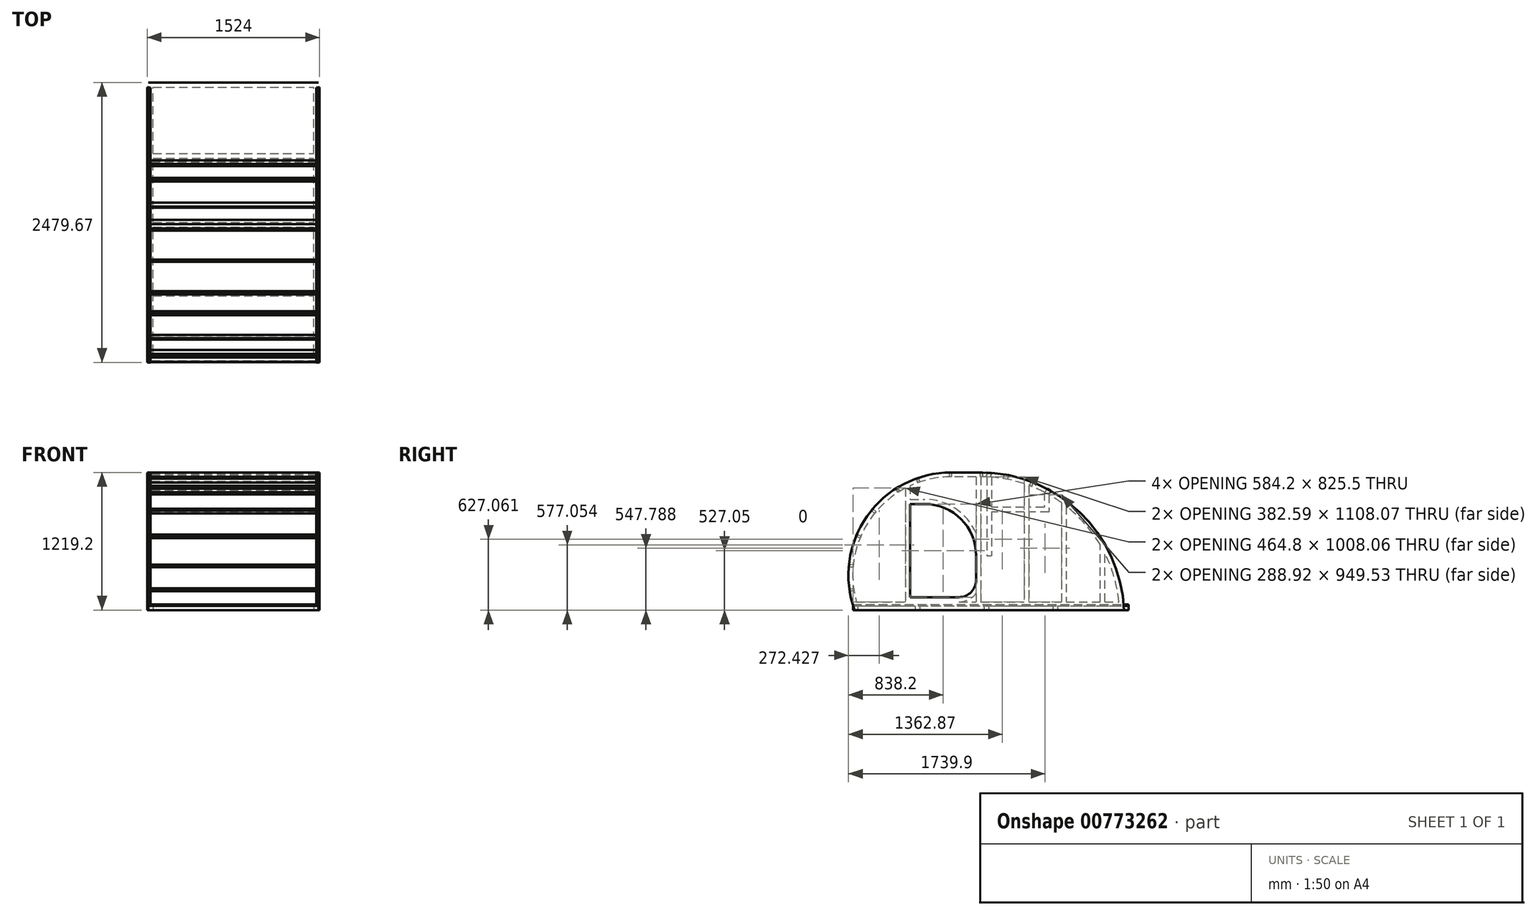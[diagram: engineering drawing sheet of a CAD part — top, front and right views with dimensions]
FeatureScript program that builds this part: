
annotation { "Feature Type Name" : "Feature", "Feature Type Description" : "" }
export const myFeature = defineFeature(function(context is Context, id is Id, definition is map)
    precondition{}
    {
        {
            var Q0;
            Q0=qCreatedBy(makeId("Right.planeOp"),FACE);
            cPlane(context, id + "F0", {"entities" : qUnion([Q0]), "cplaneType" : CPlaneType.OFFSET, "offset" : 762 * mm, "width" : 152.4 * mm, "height" : 152.4 * mm});
        }
        {
            var Q0;
            Q0=qCreatedBy(id+"F0.planeOp",FACE);
            var sketch = newSketch(context, id + "F1", { "sketchPlane" : qUnion([Q0])});
            skLineSegment(sketch, "E0", {"start": v(53.97, 0) * mm, "end": v(2438.4, 0) * mm});
            skLineSegment(sketch, "E1", {"start": v(1168.4, 1219.2) * mm, "end": v(910.4, 1219.2) * mm});
            skArc(sketch, "E2", {"start": v(910.4, 1219.2) * mm, "mid": v(165.42, 832.1) * mm, "end": v(53.97, 0) * mm});
            skLineSegment(sketch, "E3", {"start": v(0, 0) * mm, "end": v(0, 308.8) * mm, "construction": true});
            skArc(sketch, "E4", {"start": v(2438.4, 0) * mm, "mid": v(2048.65, 865.07) * mm, "end": v(1168.4, 1219.2) * mm});
            skLineSegment(sketch, "E5", {"start": v(546.1, 939.8) * mm, "end": v(546.1, 114.3) * mm});
            skLineSegment(sketch, "E6", {"start": v(546.1, 114.3) * mm, "end": v(977.9, 114.3) * mm});
            skLineSegment(sketch, "E7", {"start": v(546.1, 939.8) * mm, "end": v(673.1, 939.8) * mm});
            skLineSegment(sketch, "E8", {"start": v(1130.3, 482.6) * mm, "end": v(1130.3, 266.7) * mm});
            skArc(sketch, "E9", {"start": v(977.9, 114.3) * mm, "mid": v(1085.66, 158.94) * mm, "end": v(1130.3, 266.7) * mm});
            skArc(sketch, "E10", {"start": v(1130.3, 482.6) * mm, "mid": v(996.39, 805.89) * mm, "end": v(673.1, 939.8) * mm});
            skSolve(sketch);
        }
        {
            var Q0;
            Q0=makeQuery(id+"F1.imprint","IMPRINT",FACE,{"disambiguationData":[TD([[makeQuery(id+"F1.imprint","IMPRINT",EDGE,{"derivedFrom":sQuery(id+"F1.wireOp",EDGE,"E0")}),1.0]])]});
            extrude(context, id + "F2", {"entities" : qUnion([Q0]), "oppositeDirection" : true, "depth" : 9.52 * mm, "offsetDistance" : 25.4 * mm});
        }
        {
            var Q0;
            Q0=makeQuery(id+"F2.opExtrude","SWEPT_BODY",BODY,{"disambiguationData":[OSD([sQuery(id+"F1.wireOp",EDGE,"E0"),sQuery(id+"F1.wireOp",EDGE,"E1"),sQuery(id+"F1.wireOp",EDGE,"E2"),sQuery(id+"F1.wireOp",EDGE,"E4"),sQuery(id+"F1.wireOp",EDGE,"E5"),sQuery(id+"F1.wireOp",EDGE,"E6"),sQuery(id+"F1.wireOp",EDGE,"E7"),sQuery(id+"F1.wireOp",EDGE,"E8"),sQuery(id+"F1.wireOp",EDGE,"E9"),sQuery(id+"F1.wireOp",EDGE,"E10")])]});
            var Q1;
            Q1=qCreatedBy(makeId("Right.planeOp"),FACE);
            mirror(context, id + "F3", {"entities" : qUnion([Q0]), "mirrorPlane" : qUnion([Q1])});
        }
        {
            var Q0;
            Q0=qCreatedBy(makeId("Top.planeOp"),FACE);
            var sketch = newSketch(context, id + "F4", { "sketchPlane" : qUnion([Q0])});
            skLineSegment(sketch, "E11.bottom", {"start": v(-752.47, 41.27) * mm, "end": v(752.47, 41.27) * mm});
            skLineSegment(sketch, "E11.top", {"start": v(-752.48, 2479.68) * mm, "end": v(752.48, 2479.68) * mm});
            skLineSegment(sketch, "E11.left", {"start": v(-752.47, 41.27) * mm, "end": v(-752.48, 2479.68) * mm});
            skLineSegment(sketch, "E11.right", {"start": v(752.47, 41.27) * mm, "end": v(752.48, 2479.68) * mm});
            skLineSegment(sketch, "E12", {"start": v(0, 0) * mm, "end": v(0, 2479.68) * mm, "construction": true});
            skLineSegment(sketch, "E13.0", {"start": v(-711.2, 82.55) * mm, "end": v(711.2, 82.55) * mm});
            skLineSegment(sketch, "E14.0", {"start": v(-711.2, 82.55) * mm, "end": v(-711.2, 1198.56) * mm});
            skLineSegment(sketch, "E15.0", {"start": v(711.2, 82.55) * mm, "end": v(711.2, 588.96) * mm});
            skLineSegment(sketch, "E16.0", {"start": v(-711.2, 2438.4) * mm, "end": v(711.2, 2438.4) * mm});
            skLineSegment(sketch, "E17", {"start": v(-711.2, 609.6) * mm, "end": v(711.2, 609.6) * mm, "construction": true});
            skLineSegment(sketch, "E18", {"start": v(-711.2, 1219.2) * mm, "end": v(711.2, 1219.2) * mm, "construction": true});
            skPoint(sketch, "E18.endSnap0", {"position": v(711.2, 1260.47) * mm});
            skLineSegment(sketch, "E19", {"start": v(-711.2, 1828.8) * mm, "end": v(711.2, 1828.8) * mm, "construction": true});
            skPoint(sketch, "E20.orphan", {"position": v(711.2, 2479.68) * mm});
            skPoint(sketch, "E21.orphan", {"position": v(711.2, 41.27) * mm});
            skLineSegment(sketch, "E22.0", {"start": v(-711.2, 588.96) * mm, "end": v(711.2, 588.96) * mm});
            skLineSegment(sketch, "E23.0", {"start": v(-711.2, 630.24) * mm, "end": v(711.2, 630.24) * mm});
            skLineSegment(sketch, "E24.0", {"start": v(-711.2, 1808.16) * mm, "end": v(711.2, 1808.16) * mm});
            skLineSegment(sketch, "E25.0", {"start": v(-711.2, 1849.44) * mm, "end": v(711.2, 1849.44) * mm});
            skLineSegment(sketch, "E26.0", {"start": v(-711.2, 1239.84) * mm, "end": v(711.2, 1239.84) * mm});
            skLineSegment(sketch, "E27.0", {"start": v(-711.2, 1198.56) * mm, "end": v(711.2, 1198.56) * mm});
            skLineSegment(sketch, "E28.trimOffspring", {"start": v(-711.2, 1849.44) * mm, "end": v(-711.2, 2438.4) * mm});
            skLineSegment(sketch, "E29.trimOffspring", {"start": v(-711.2, 1239.84) * mm, "end": v(-711.2, 1808.16) * mm});
            skLineSegment(sketch, "E30.trimOffspring", {"start": v(711.2, 1849.44) * mm, "end": v(711.2, 2438.4) * mm});
            skLineSegment(sketch, "E31.trimOffspring", {"start": v(711.2, 1239.84) * mm, "end": v(711.2, 1808.16) * mm});
            skLineSegment(sketch, "E32.trimOffspring", {"start": v(711.2, 630.24) * mm, "end": v(711.2, 1198.56) * mm});
            skSolve(sketch);
        }
        {
            var Q0;
            Q0 = qSketchRegion(id + "F4", true);
            extrude(context, id + "F5", {"entities" : qUnion([Q0]), "depth" : 38.1 * mm, "offsetDistance" : 25.4 * mm});
        }
        {
            var Q0;
            Q0=makeQuery(id+"F5.opExtrude","CAP_FACE",FACE,{"disambiguationData":[OSD([sQuery(id+"F4.wireOp",EDGE,"E11.bottom"),sQuery(id+"F4.wireOp",EDGE,"E11.top"),sQuery(id+"F4.wireOp",EDGE,"E11.left"),sQuery(id+"F4.wireOp",EDGE,"E11.right"),sQuery(id+"F4.wireOp",EDGE,"E13.0"),sQuery(id+"F4.wireOp",EDGE,"E14.0"),sQuery(id+"F4.wireOp",EDGE,"E15.0"),sQuery(id+"F4.wireOp",EDGE,"E16.0"),sQuery(id+"F4.wireOp",EDGE,"E22.0"),sQuery(id+"F4.wireOp",EDGE,"E23.0"),sQuery(id+"F4.wireOp",EDGE,"E24.0"),sQuery(id+"F4.wireOp",EDGE,"E25.0"),sQuery(id+"F4.wireOp",EDGE,"E26.0"),sQuery(id+"F4.wireOp",EDGE,"E27.0"),sQuery(id+"F4.wireOp",EDGE,"E28.trimOffspring"),sQuery(id+"F4.wireOp",EDGE,"E29.trimOffspring"),sQuery(id+"F4.wireOp",EDGE,"E30.trimOffspring"),sQuery(id+"F4.wireOp",EDGE,"E31.trimOffspring"),sQuery(id+"F4.wireOp",EDGE,"E32.trimOffspring")])],"isStart":false});
            var sketch = newSketch(context, id + "F6", { "sketchPlane" : qUnion([Q0])});
            skLineSegment(sketch, "E33.bottom", {"start": v(752.48, 2479.68) * mm, "end": v(-752.47, 2479.68) * mm});
            skLineSegment(sketch, "E33.top", {"start": v(752.48, 41.27) * mm, "end": v(-752.47, 41.27) * mm});
            skLineSegment(sketch, "E33.left", {"start": v(752.48, 2479.68) * mm, "end": v(752.48, 41.27) * mm});
            skLineSegment(sketch, "E33.right", {"start": v(-752.47, 2479.68) * mm, "end": v(-752.47, 41.27) * mm});
            skSolve(sketch);
        }
        {
            var Q0;
            Q0 = qSketchRegion(id + "F6", true);
            extrude(context, id + "F7", {"entities" : qUnion([Q0]), "depth" : 12.7 * mm, "offsetDistance" : 25.4 * mm});
        }
        {
            var Q0;
            Q0=makeQuery(id+"F3.opPattern","COPY",FACE,{"derivedFrom":makeQuery(id+"F2.opExtrude","CAP_FACE",FACE,{"disambiguationData":[OSD([sQuery(id+"F1.wireOp",EDGE,"E0"),sQuery(id+"F1.wireOp",EDGE,"E1"),sQuery(id+"F1.wireOp",EDGE,"E2"),sQuery(id+"F1.wireOp",EDGE,"E4"),sQuery(id+"F1.wireOp",EDGE,"E5"),sQuery(id+"F1.wireOp",EDGE,"E6"),sQuery(id+"F1.wireOp",EDGE,"E7"),sQuery(id+"F1.wireOp",EDGE,"E8"),sQuery(id+"F1.wireOp",EDGE,"E9"),sQuery(id+"F1.wireOp",EDGE,"E10")])],"isStart":false}),"instanceName":"1"});
            var sketch = newSketch(context, id + "F8", { "sketchPlane" : qUnion([Q0])});
            skArc(sketch, "E34.0", {"start": v(910.4, 1181.1) * mm, "mid": v(723.94, 1160.94) * mm, "end": v(546.1, 1101.39) * mm});
            skArc(sketch, "E35.0", {"start": v(910.4, 1219.2) * mm, "mid": v(181.1, 853.75) * mm, "end": v(37.33, 50.8) * mm});
            skLineSegment(sketch, "E36.0", {"start": v(37.33, 50.8) * mm, "end": v(2435.3, 50.8) * mm});
            skLineSegment(sketch, "E37.0", {"start": v(1130.3, 1181.1) * mm, "end": v(910.4, 1181.1) * mm});
            skArc(sketch, "E38.0", {"start": v(2395.02, 73.03) * mm, "mid": v(2351.64, 294.74) * mm, "end": v(2268.54, 504.81) * mm});
            skLineSegment(sketch, "E39.0", {"start": v(1168.4, 1219.2) * mm, "end": v(910.4, 1219.2) * mm});
            skArc(sketch, "E40.0", {"start": v(2411.06, 215.34) * mm, "mid": v(1967.14, 936.88) * mm, "end": v(1168.4, 1219.2) * mm});
            skPoint(sketch, "E41.orphan", {"position": v(2479.68, 50.8) * mm});
            skPoint(sketch, "E42.orphan", {"position": v(41.27, 50.8) * mm});
            skPoint(sketch, "E43.orphan", {"position": v(53.97, 0) * mm});
            skLineSegment(sketch, "E44.0", {"start": v(504.82, 1081.08) * mm, "end": v(504.82, 73.03) * mm});
            skArc(sketch, "E45.0", {"start": v(1171.58, 482.6) * mm, "mid": v(1025.58, 835.08) * mm, "end": v(673.1, 981.08) * mm});
            skLineSegment(sketch, "E46.0", {"start": v(504.82, 981.08) * mm, "end": v(673.1, 981.08) * mm});
            skLineSegment(sketch, "E47.0", {"start": v(1171.58, 1181.1) * mm, "end": v(1171.58, 73.03) * mm});
            skArc(sketch, "E48.0", {"start": v(977.9, 73.03) * mm, "mid": v(1114.85, 129.75) * mm, "end": v(1171.58, 266.7) * mm});
            skLineSegment(sketch, "E49.0", {"start": v(70.57, 73.03) * mm, "end": v(1130.3, 73.03) * mm});
            skLineSegment(sketch, "E50.0", {"start": v(546.1, 1101.39) * mm, "end": v(546.1, 981.08) * mm});
            skLineSegment(sketch, "E50.1", {"start": v(546.1, 939.8) * mm, "end": v(673.1, 939.8) * mm});
            skArc(sketch, "E50.2", {"start": v(1130.3, 482.6) * mm, "mid": v(996.39, 805.89) * mm, "end": v(673.1, 939.8) * mm});
            skLineSegment(sketch, "E50.3", {"start": v(1130.3, 1181.1) * mm, "end": v(1130.3, 681.2) * mm});
            skArc(sketch, "E50.4", {"start": v(977.9, 114.3) * mm, "mid": v(1085.66, 158.94) * mm, "end": v(1130.3, 266.7) * mm});
            skLineSegment(sketch, "E50.5", {"start": v(546.1, 114.3) * mm, "end": v(977.9, 114.3) * mm});
            skLineSegment(sketch, "E51", {"start": v(977.9, 73.03) * mm, "end": v(504.82, 73.03) * mm});
            skLineSegment(sketch, "E52.trimOffspring", {"start": v(1130.3, 482.6) * mm, "end": v(1130.3, 266.7) * mm});
            skLineSegment(sketch, "E53.trimOffspring", {"start": v(546.1, 939.8) * mm, "end": v(546.1, 114.3) * mm});
            skLineSegment(sketch, "E54.trimOffspring", {"start": v(1130.3, 147.18) * mm, "end": v(1130.3, 73.03) * mm});
            skLineSegment(sketch, "E55", {"start": v(1595.44, 1104.79) * mm, "end": v(1595.44, 909.64) * mm});
            skLineSegment(sketch, "E56", {"start": v(1554.16, 1119.2) * mm, "end": v(1554.16, 909.64) * mm});
            skLineSegment(sketch, "E57", {"start": v(1574.8, 73.03) * mm, "end": v(1574.8, 1112.2) * mm, "construction": true});
            skLineSegment(sketch, "E58.left", {"start": v(1223.96, 1179.85) * mm, "end": v(1223.96, 482.6) * mm});
            skLineSegment(sketch, "E58.right", {"start": v(1265.24, 1177.3) * mm, "end": v(1265.24, 482.6) * mm});
            skLineSegment(sketch, "E59", {"start": v(1244.6, 1178.74) * mm, "end": v(1244.6, 482.6) * mm, "construction": true});
            skLineSegment(sketch, "E60", {"start": v(1223.96, 482.6) * mm, "end": v(1265.24, 482.6) * mm});
            skLineSegment(sketch, "E61", {"start": v(1752.6, 1033.91) * mm, "end": v(1752.6, 889) * mm, "construction": true});
            skLineSegment(sketch, "E62", {"start": v(1905, 936.88) * mm, "end": v(1905, 50.8) * mm, "construction": true});
            skPoint(sketch, "E62.startSnap0", {"position": v(1967.14, 936.88) * mm});
            skLineSegment(sketch, "E63", {"start": v(1773.24, 868.36) * mm, "end": v(1595.44, 868.36) * mm});
            skLineSegment(sketch, "E64.0", {"start": v(1752.6, 889) * mm, "end": v(1244.6, 889) * mm, "construction": true});
            skLineSegment(sketch, "E65.0", {"start": v(1773.24, 1022.55) * mm, "end": v(1773.24, 868.36) * mm});
            skLineSegment(sketch, "E66.0", {"start": v(1731.96, 1044.77) * mm, "end": v(1731.96, 909.64) * mm});
            skLineSegment(sketch, "E67.0", {"start": v(1731.96, 909.64) * mm, "end": v(1595.44, 909.64) * mm});
            skLineSegment(sketch, "E68.0", {"start": v(1884.36, 951.93) * mm, "end": v(1884.36, 73.03) * mm});
            skLineSegment(sketch, "E69.0", {"start": v(1925.64, 921.17) * mm, "end": v(1925.64, 73.03) * mm});
            skLineSegment(sketch, "E70.trimOffspring", {"start": v(1595.44, 868.36) * mm, "end": v(1595.44, 73.03) * mm});
            skLineSegment(sketch, "E71.trimOffspring", {"start": v(1554.16, 868.36) * mm, "end": v(1265.24, 868.36) * mm});
            skLineSegment(sketch, "E72.trimOffspring", {"start": v(1554.16, 868.36) * mm, "end": v(1554.16, 73.03) * mm});
            skLineSegment(sketch, "E73.trimOffspring", {"start": v(1554.16, 909.64) * mm, "end": v(1265.24, 909.64) * mm});
            skLineSegment(sketch, "E74", {"start": v(2247.9, 73.03) * mm, "end": v(2247.9, 543.85) * mm, "construction": true});
            skLineSegment(sketch, "E75.0", {"start": v(2268.54, 73.03) * mm, "end": v(2268.54, 504.81) * mm});
            skLineSegment(sketch, "E76.0", {"start": v(2227.26, 73.03) * mm, "end": v(2227.26, 579.8) * mm});
            skArc(sketch, "E77.trimOffspring", {"start": v(504.82, 1081.08) * mm, "mid": v(109.27, 653.92) * mm, "end": v(70.57, 73.02) * mm});
            skArc(sketch, "E78.trimOffspring", {"start": v(1223.96, 1179.85) * mm, "mid": v(1197.78, 1180.75) * mm, "end": v(1171.58, 1181.1) * mm});
            skArc(sketch, "E79.trimOffspring", {"start": v(1554.16, 1119.2) * mm, "mid": v(1411.44, 1156.9) * mm, "end": v(1265.24, 1177.3) * mm});
            skArc(sketch, "E80.trimOffspring", {"start": v(1731.96, 1044.77) * mm, "mid": v(1664.6, 1076.84) * mm, "end": v(1595.44, 1104.79) * mm});
            skArc(sketch, "E81.trimOffspring", {"start": v(1884.36, 951.93) * mm, "mid": v(1829.74, 988.72) * mm, "end": v(1773.24, 1022.55) * mm});
            skArc(sketch, "E82.trimOffspring", {"start": v(2227.26, 579.8) * mm, "mid": v(2092.35, 764.54) * mm, "end": v(1925.64, 921.17) * mm});
            skLineSegment(sketch, "E83.trimOffspring", {"start": v(2268.54, 73.03) * mm, "end": v(2395.02, 73.03) * mm});
            skLineSegment(sketch, "E84.trimOffspring", {"start": v(1925.64, 73.03) * mm, "end": v(2227.26, 73.03) * mm});
            skLineSegment(sketch, "E85.trimOffspring", {"start": v(1595.44, 73.03) * mm, "end": v(1884.36, 73.03) * mm});
            skLineSegment(sketch, "E86.trimOffspring", {"start": v(1171.58, 73.03) * mm, "end": v(1554.16, 73.03) * mm});
            skSolve(sketch);
        }
        {
            var Q0;
            Q0=makeQuery(id+"F8.imprint","IMPRINT",FACE,{"disambiguationData":[TD([[makeQuery(id+"F8.imprint","IMPRINT",EDGE,{"derivedFrom":sQuery(id+"F8.wireOp",EDGE,"E34.0")}),-1.0]])]});
            var Q1;
            Q1=makeQuery(id+"F8.imprint","IMPRINT",FACE,{"disambiguationData":[TD([[makeQuery(id+"F8.imprint","IMPRINT",EDGE,{"derivedFrom":sQuery(id+"F8.wireOp",EDGE,"E50.1")}),1.0]])]});
            extrude(context, id + "F9", {"entities" : qUnion([Q0, Q1]), "depth" : 19.05 * mm, "offsetDistance" : 25.4 * mm});
        }
        {
            var Q0;
            Q0=makeQuery(id+"F9.opExtrude","SWEPT_BODY",BODY,{"disambiguationData":[OSD([sQuery(id+"F1.wireOp",EDGE,"E4"),sQuery(id+"F8.wireOp",EDGE,"E34.0"),sQuery(id+"F8.wireOp",EDGE,"E35.0"),sQuery(id+"F8.wireOp",EDGE,"E36.0"),sQuery(id+"F8.wireOp",EDGE,"E37.0"),sQuery(id+"F8.wireOp",EDGE,"E38.0"),sQuery(id+"F8.wireOp",EDGE,"E39.0"),sQuery(id+"F8.wireOp",EDGE,"E40.0"),sQuery(id+"F8.wireOp",EDGE,"E44.0"),sQuery(id+"F8.wireOp",EDGE,"E45.0"),sQuery(id+"F8.wireOp",EDGE,"E46.0"),sQuery(id+"F8.wireOp",EDGE,"E47.0"),sQuery(id+"F8.wireOp",EDGE,"E48.0"),sQuery(id+"F8.wireOp",EDGE,"E49.0"),sQuery(id+"F8.wireOp",EDGE,"E50.0"),sQuery(id+"F8.wireOp",EDGE,"E50.1"),sQuery(id+"F8.wireOp",EDGE,"E50.2"),sQuery(id+"F8.wireOp",EDGE,"E50.3"),sQuery(id+"F8.wireOp",EDGE,"E50.4"),sQuery(id+"F8.wireOp",EDGE,"E50.5"),sQuery(id+"F8.wireOp",EDGE,"E52.trimOffspring"),sQuery(id+"F8.wireOp",EDGE,"E53.trimOffspring"),sQuery(id+"F8.wireOp",EDGE,"E54.trimOffspring"),sQuery(id+"F8.wireOp",EDGE,"E55"),sQuery(id+"F8.wireOp",EDGE,"E56"),sQuery(id+"F8.wireOp",EDGE,"E58.left"),sQuery(id+"F8.wireOp",EDGE,"E58.right"),sQuery(id+"F8.wireOp",EDGE,"E60"),sQuery(id+"F8.wireOp",EDGE,"E63"),sQuery(id+"F8.wireOp",EDGE,"E65.0"),sQuery(id+"F8.wireOp",EDGE,"E66.0"),sQuery(id+"F8.wireOp",EDGE,"E67.0"),sQuery(id+"F8.wireOp",EDGE,"E68.0"),sQuery(id+"F8.wireOp",EDGE,"E69.0"),sQuery(id+"F8.wireOp",EDGE,"E70.trimOffspring"),sQuery(id+"F8.wireOp",EDGE,"E71.trimOffspring"),sQuery(id+"F8.wireOp",EDGE,"E72.trimOffspring"),sQuery(id+"F8.wireOp",EDGE,"E73.trimOffspring"),sQuery(id+"F8.wireOp",EDGE,"E75.0"),sQuery(id+"F8.wireOp",EDGE,"E76.0"),sQuery(id+"F8.wireOp",EDGE,"E77.trimOffspring"),sQuery(id+"F8.wireOp",EDGE,"E78.trimOffspring"),sQuery(id+"F8.wireOp",EDGE,"E79.trimOffspring"),sQuery(id+"F8.wireOp",EDGE,"E80.trimOffspring"),sQuery(id+"F8.wireOp",EDGE,"E81.trimOffspring"),sQuery(id+"F8.wireOp",EDGE,"E82.trimOffspring"),sQuery(id+"F8.wireOp",EDGE,"E83.trimOffspring"),sQuery(id+"F8.wireOp",EDGE,"E84.trimOffspring"),sQuery(id+"F8.wireOp",EDGE,"E85.trimOffspring"),sQuery(id+"F8.wireOp",EDGE,"E86.trimOffspring")])]});
            var Q1;
            Q1=qCreatedBy(makeId("Right.planeOp"),FACE);
            mirror(context, id + "F10", {"entities" : qUnion([Q0]), "mirrorPlane" : qUnion([Q1])});
        }
        {
            var Q0;
            Q0=makeQuery(id+"F9.opExtrude","CAP_FACE",FACE,{"disambiguationData":[OSD([sQuery(id+"F8.wireOp",EDGE,"E34.0"),sQuery(id+"F8.wireOp",EDGE,"E35.0"),sQuery(id+"F8.wireOp",EDGE,"E36.0"),sQuery(id+"F8.wireOp",EDGE,"E37.0"),sQuery(id+"F8.wireOp",EDGE,"E38.0"),sQuery(id+"F8.wireOp",EDGE,"E39.0"),sQuery(id+"F8.wireOp",EDGE,"E40.0"),sQuery(id+"F8.wireOp",EDGE,"a9486861-b13c-4b14-bedc-575190c04a62.trimOffspring")])],"isStart":false});
            var sketch = newSketch(context, id + "F11", { "sketchPlane" : qUnion([Q0])});
            skLineSegment(sketch, "E87.bottom", {"start": v(45.91, 192.33) * mm, "end": v(8.15, 187.24) * mm});
            skLineSegment(sketch, "E87.top", {"start": v(48.46, 173.45) * mm, "end": v(10.7, 168.36) * mm});
            skLineSegment(sketch, "E87.left", {"start": v(45.91, 192.33) * mm, "end": v(48.46, 173.45) * mm});
            skLineSegment(sketch, "E87.right", {"start": v(8.15, 187.24) * mm, "end": v(10.7, 168.36) * mm});
            skPoint(sketch, "E87.middle", {"position": v(28.3, 180.34) * mm});
            skPoint(sketch, "E88", {"position": v(9.43, 177.8) * mm});
            skLineSegment(sketch, "E89.bottom", {"start": v(4.9, 403.17) * mm, "end": v(42.8, 399.22) * mm});
            skLineSegment(sketch, "E89.top", {"start": v(2.93, 384.23) * mm, "end": v(40.82, 380.28) * mm});
            skLineSegment(sketch, "E89.left", {"start": v(4.9, 403.17) * mm, "end": v(2.93, 384.23) * mm});
            skLineSegment(sketch, "E89.right", {"start": v(42.8, 399.22) * mm, "end": v(40.82, 380.28) * mm});
            skPoint(sketch, "E89.middle", {"position": v(22.86, 391.73) * mm});
            skPoint(sketch, "E90", {"position": v(3.92, 393.7) * mm});
            skLineSegment(sketch, "E91.bottom", {"start": v(74.16, 669.22) * mm, "end": v(109.46, 654.88) * mm});
            skLineSegment(sketch, "E91.top", {"start": v(67, 651.58) * mm, "end": v(102.29, 637.23) * mm});
            skLineSegment(sketch, "E91.left", {"start": v(74.16, 669.22) * mm, "end": v(67, 651.58) * mm});
            skLineSegment(sketch, "E91.right", {"start": v(109.46, 654.88) * mm, "end": v(102.29, 637.23) * mm});
            skPoint(sketch, "E91.middle", {"position": v(88.23, 653.23) * mm});
            skPoint(sketch, "E92", {"position": v(70.58, 660.4) * mm});
            skLineSegment(sketch, "E93.bottom", {"start": v(232.12, 857.38) * mm, "end": v(202.76, 881.66) * mm});
            skLineSegment(sketch, "E93.top", {"start": v(244.26, 872.06) * mm, "end": v(214.9, 896.34) * mm});
            skLineSegment(sketch, "E93.left", {"start": v(232.12, 857.38) * mm, "end": v(244.26, 872.06) * mm});
            skLineSegment(sketch, "E93.right", {"start": v(202.76, 881.66) * mm, "end": v(214.9, 896.34) * mm});
            skPoint(sketch, "E93.middle", {"position": v(223.5, 876.86) * mm});
            skPoint(sketch, "E94", {"position": v(208.83, 889) * mm});
            skLineSegment(sketch, "E95.bottom", {"start": v(438, 1042.18) * mm, "end": v(454.12, 1052.32) * mm});
            skLineSegment(sketch, "E95.top", {"start": v(417.72, 1074.43) * mm, "end": v(433.84, 1084.57) * mm});
            skLineSegment(sketch, "E95.left", {"start": v(438, 1042.18) * mm, "end": v(417.72, 1074.43) * mm});
            skLineSegment(sketch, "E95.right", {"start": v(454.12, 1052.32) * mm, "end": v(433.84, 1084.57) * mm});
            skPoint(sketch, "E95.middle", {"position": v(435.92, 1063.37) * mm});
            skPoint(sketch, "E96", {"position": v(425.78, 1079.5) * mm});
            skLineSegment(sketch, "E97.bottom", {"start": v(632.07, 1135.56) * mm, "end": v(614.09, 1129.29) * mm});
            skLineSegment(sketch, "E97.top", {"start": v(619.53, 1171.54) * mm, "end": v(601.54, 1165.26) * mm});
            skLineSegment(sketch, "E97.left", {"start": v(632.07, 1135.56) * mm, "end": v(619.53, 1171.54) * mm});
            skLineSegment(sketch, "E97.right", {"start": v(614.09, 1129.29) * mm, "end": v(601.54, 1165.26) * mm});
            skPoint(sketch, "E97.middle", {"position": v(616.8, 1150.41) * mm});
            skPoint(sketch, "E98", {"position": v(610.53, 1168.4) * mm});
            skLineSegment(sketch, "E99.bottom", {"start": v(891.74, 1180.9) * mm, "end": v(910.79, 1181.1) * mm});
            skLineSegment(sketch, "E99.top", {"start": v(891.34, 1219) * mm, "end": v(910.4, 1219.2) * mm});
            skLineSegment(sketch, "E99.left", {"start": v(891.74, 1180.9) * mm, "end": v(891.34, 1219) * mm});
            skLineSegment(sketch, "E99.right", {"start": v(910.79, 1181.1) * mm, "end": v(910.4, 1219.2) * mm});
            skPoint(sketch, "E99.middle", {"position": v(901.07, 1200.05) * mm});
            skLineSegment(sketch, "E100.bottom", {"start": v(1168.4, 1219.2) * mm, "end": v(1187.45, 1219.2) * mm});
            skLineSegment(sketch, "E100.top", {"start": v(1168.4, 1181.1) * mm, "end": v(1187.45, 1181.1) * mm});
            skLineSegment(sketch, "E100.left", {"start": v(1168.4, 1219.2) * mm, "end": v(1168.4, 1181.1) * mm});
            skLineSegment(sketch, "E100.right", {"start": v(1187.45, 1219.2) * mm, "end": v(1187.45, 1181.1) * mm});
            skLineSegment(sketch, "E101.bottom", {"start": v(1244.6, 1216.91) * mm, "end": v(1263.62, 1215.77) * mm});
            skLineSegment(sketch, "E101.top", {"start": v(1242.32, 1178.88) * mm, "end": v(1261.33, 1177.74) * mm});
            skLineSegment(sketch, "E101.left", {"start": v(1244.6, 1216.91) * mm, "end": v(1242.32, 1178.88) * mm});
            skLineSegment(sketch, "E101.right", {"start": v(1263.62, 1215.77) * mm, "end": v(1261.33, 1177.74) * mm});
            skLineSegment(sketch, "E102.bottom", {"start": v(1244.6, 1216.91) * mm, "end": v(1225.58, 1218.06) * mm});
            skLineSegment(sketch, "E102.top", {"start": v(1242.32, 1178.88) * mm, "end": v(1223.3, 1180.02) * mm});
            skLineSegment(sketch, "E102.right", {"start": v(1225.58, 1218.06) * mm, "end": v(1223.3, 1180.02) * mm});
            skLineSegment(sketch, "E103.bottom", {"start": v(1397, 1198.47) * mm, "end": v(1415.74, 1195.05) * mm});
            skLineSegment(sketch, "E103.top", {"start": v(1390.15, 1161) * mm, "end": v(1408.89, 1157.57) * mm});
            skLineSegment(sketch, "E103.left", {"start": v(1397, 1198.47) * mm, "end": v(1390.15, 1161) * mm});
            skLineSegment(sketch, "E103.right", {"start": v(1415.74, 1195.05) * mm, "end": v(1408.89, 1157.57) * mm});
            skLineSegment(sketch, "E104.bottom", {"start": v(1616.71, 1137.55) * mm, "end": v(1634.49, 1130.7) * mm});
            skLineSegment(sketch, "E104.top", {"start": v(1603, 1102) * mm, "end": v(1620.78, 1095.15) * mm});
            skLineSegment(sketch, "E104.left", {"start": v(1616.71, 1137.55) * mm, "end": v(1603, 1102) * mm});
            skLineSegment(sketch, "E104.right", {"start": v(1634.49, 1130.7) * mm, "end": v(1620.78, 1095.15) * mm});
            skPoint(sketch, "E105", {"position": v(1625.6, 1134.13) * mm});
            skLineSegment(sketch, "E106.bottom", {"start": v(1378.26, 1201.9) * mm, "end": v(1397, 1198.47) * mm});
            skLineSegment(sketch, "E106.top", {"start": v(1371.4, 1164.42) * mm, "end": v(1390.15, 1161) * mm});
            skLineSegment(sketch, "E106.left", {"start": v(1378.26, 1201.9) * mm, "end": v(1371.4, 1164.42) * mm});
            skLineSegment(sketch, "E107.bottom", {"start": v(1773.06, 1023.33) * mm, "end": v(1756.17, 1032.15) * mm});
            skLineSegment(sketch, "E107.top", {"start": v(1790.7, 1057.1) * mm, "end": v(1773.82, 1065.92) * mm});
            skLineSegment(sketch, "E108.bottom", {"start": v(1773.82, 1065.92) * mm, "end": v(1756.93, 1074.74) * mm});
            skLineSegment(sketch, "E108.top", {"start": v(1756.17, 1032.15) * mm, "end": v(1739.29, 1040.97) * mm});
            skLineSegment(sketch, "E108.left", {"start": v(1773.82, 1065.92) * mm, "end": v(1756.17, 1032.15) * mm});
            skLineSegment(sketch, "E108.right", {"start": v(1756.93, 1074.74) * mm, "end": v(1739.29, 1040.97) * mm});
            skLineSegment(sketch, "E109", {"start": v(1773.06, 1023.33) * mm, "end": v(1790.7, 1057.1) * mm});
            skSolve(sketch);
        }
        {
            var Q0;
            Q0 = qSketchRegion(id + "F11", true);
            var Q1;
            Q1=makeQuery(id+"F10.opPattern","COPY",FACE,{"derivedFrom":makeQuery(id+"F9.opExtrude","CAP_FACE",FACE,{"disambiguationData":[OSD([sQuery(id+"F1.wireOp",EDGE,"E4"),sQuery(id+"F8.wireOp",EDGE,"E34.0"),sQuery(id+"F8.wireOp",EDGE,"E35.0"),sQuery(id+"F8.wireOp",EDGE,"E36.0"),sQuery(id+"F8.wireOp",EDGE,"E37.0"),sQuery(id+"F8.wireOp",EDGE,"E38.0"),sQuery(id+"F8.wireOp",EDGE,"E39.0"),sQuery(id+"F8.wireOp",EDGE,"E40.0"),sQuery(id+"F8.wireOp",EDGE,"E44.0"),sQuery(id+"F8.wireOp",EDGE,"E45.0"),sQuery(id+"F8.wireOp",EDGE,"E46.0"),sQuery(id+"F8.wireOp",EDGE,"E47.0"),sQuery(id+"F8.wireOp",EDGE,"E48.0"),sQuery(id+"F8.wireOp",EDGE,"E49.0"),sQuery(id+"F8.wireOp",EDGE,"E50.0"),sQuery(id+"F8.wireOp",EDGE,"E50.1"),sQuery(id+"F8.wireOp",EDGE,"E50.2"),sQuery(id+"F8.wireOp",EDGE,"E50.3"),sQuery(id+"F8.wireOp",EDGE,"E50.4"),sQuery(id+"F8.wireOp",EDGE,"E50.5"),sQuery(id+"F8.wireOp",EDGE,"E52.trimOffspring"),sQuery(id+"F8.wireOp",EDGE,"E53.trimOffspring"),sQuery(id+"F8.wireOp",EDGE,"E54.trimOffspring"),sQuery(id+"F8.wireOp",EDGE,"E55"),sQuery(id+"F8.wireOp",EDGE,"E56"),sQuery(id+"F8.wireOp",EDGE,"E58.left"),sQuery(id+"F8.wireOp",EDGE,"E58.right"),sQuery(id+"F8.wireOp",EDGE,"E60"),sQuery(id+"F8.wireOp",EDGE,"E63"),sQuery(id+"F8.wireOp",EDGE,"E65.0"),sQuery(id+"F8.wireOp",EDGE,"E66.0"),sQuery(id+"F8.wireOp",EDGE,"E67.0"),sQuery(id+"F8.wireOp",EDGE,"E68.0"),sQuery(id+"F8.wireOp",EDGE,"E69.0"),sQuery(id+"F8.wireOp",EDGE,"E70.trimOffspring"),sQuery(id+"F8.wireOp",EDGE,"E71.trimOffspring"),sQuery(id+"F8.wireOp",EDGE,"E72.trimOffspring"),sQuery(id+"F8.wireOp",EDGE,"E73.trimOffspring"),sQuery(id+"F8.wireOp",EDGE,"E75.0"),sQuery(id+"F8.wireOp",EDGE,"E76.0"),sQuery(id+"F8.wireOp",EDGE,"E77.trimOffspring"),sQuery(id+"F8.wireOp",EDGE,"E78.trimOffspring"),sQuery(id+"F8.wireOp",EDGE,"E79.trimOffspring"),sQuery(id+"F8.wireOp",EDGE,"E80.trimOffspring"),sQuery(id+"F8.wireOp",EDGE,"E81.trimOffspring"),sQuery(id+"F8.wireOp",EDGE,"E82.trimOffspring"),sQuery(id+"F8.wireOp",EDGE,"E83.trimOffspring"),sQuery(id+"F8.wireOp",EDGE,"E84.trimOffspring"),sQuery(id+"F8.wireOp",EDGE,"E85.trimOffspring"),sQuery(id+"F8.wireOp",EDGE,"E86.trimOffspring")])],"isStart":false}),"instanceName":"1"});
            extrude(context, id + "F12", {"entities" : qUnion([Q0]), "endBound" : BoundingType.UP_TO_SURFACE, "depth" : 25.4 * mm, "endBoundEntityFace" : qUnion([Q1]), "offsetDistance" : 25.4 * mm});
        }
    });
